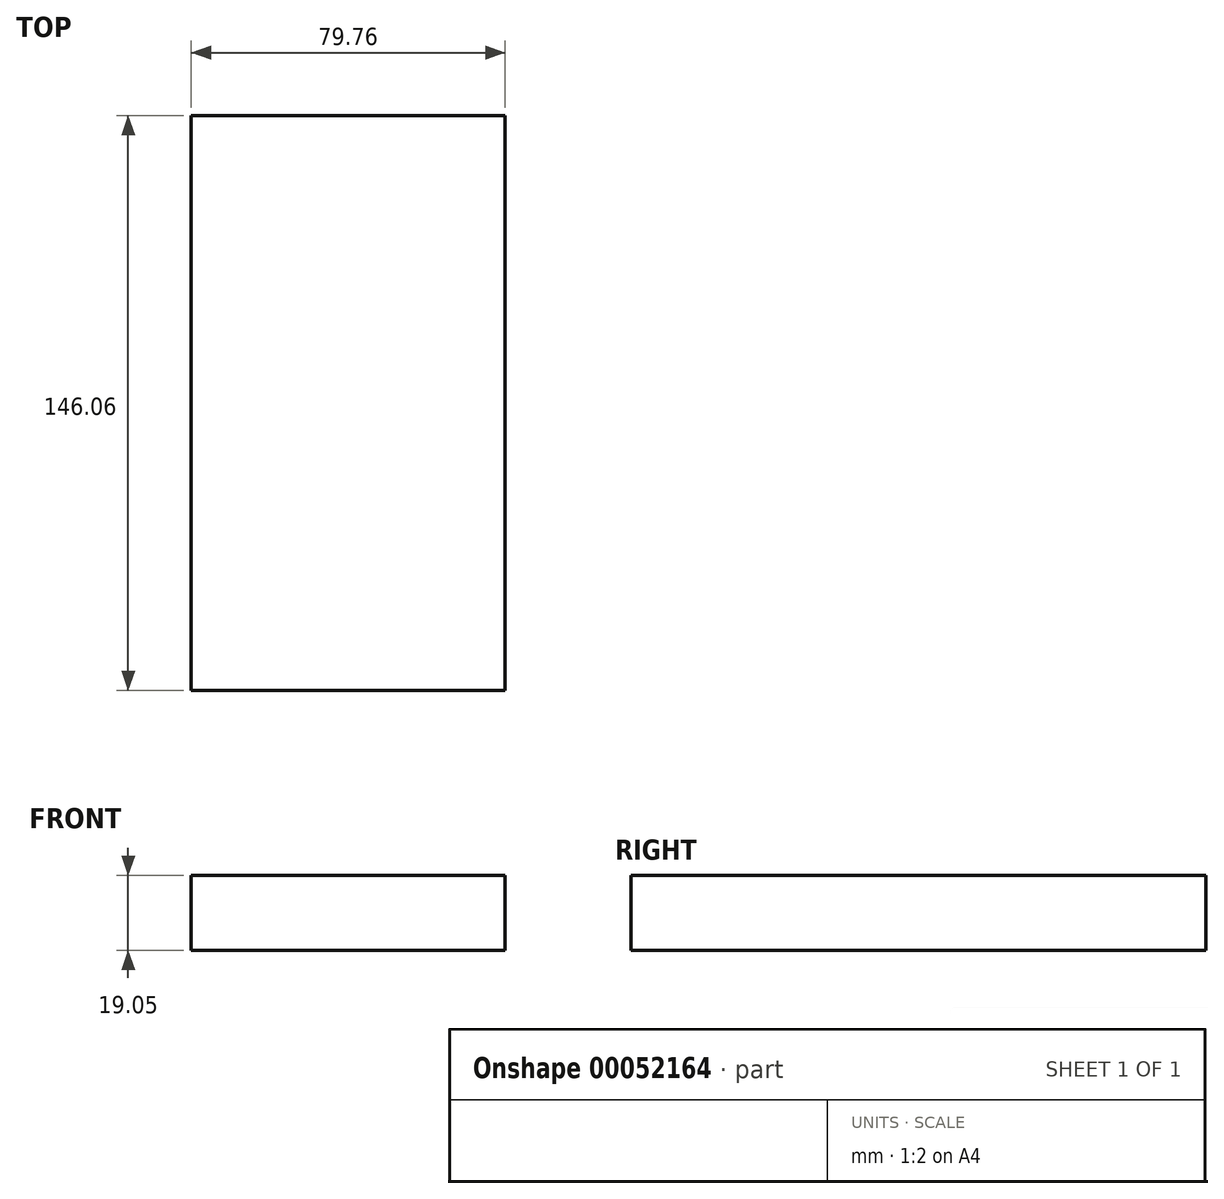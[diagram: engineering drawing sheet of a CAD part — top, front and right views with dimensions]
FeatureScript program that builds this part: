
annotation { "Feature Type Name" : "Feature", "Feature Type Description" : "" }
export const myFeature = defineFeature(function(context is Context, id is Id, definition is map)
    precondition{}
    {
        {
            var Q0;
            Q0=qCreatedBy(makeId("Top.planeOp"),FACE);
            var sketch = newSketch(context, id + "F0", { "sketchPlane" : qUnion([Q0])});
            skLineSegment(sketch, "E0.rect.bottom", {"start": v(39.88, 73.03) * mm, "end": v(-39.88, 73.03) * mm});
            skLineSegment(sketch, "E0.rect.top", {"start": v(39.88, -73.03) * mm, "end": v(-39.88, -73.03) * mm});
            skLineSegment(sketch, "E0.rect.left", {"start": v(39.88, 73.03) * mm, "end": v(39.88, -73.03) * mm});
            skLineSegment(sketch, "E0.rect.right", {"start": v(-39.88, 73.03) * mm, "end": v(-39.88, -73.03) * mm});
            skPoint(sketch, "E0.rect.middle", {"position": v(0, 0) * mm});
            skSolve(sketch);
        }
        {
            var Q0;
            Q0=makeQuery(id+"F0.imprint","IMPRINT",FACE,{"disambiguationData":[TD([[makeQuery(id+"F0.imprint","IMPRINT",EDGE,{"derivedFrom":sQuery(id+"F0.wireOp",EDGE,"E0.rect.bottom")}),1.0]])]});
            extrude(context, id + "F1", {"entities" : qUnion([Q0]), "depth" : 19.05 * mm});
        }
    });
